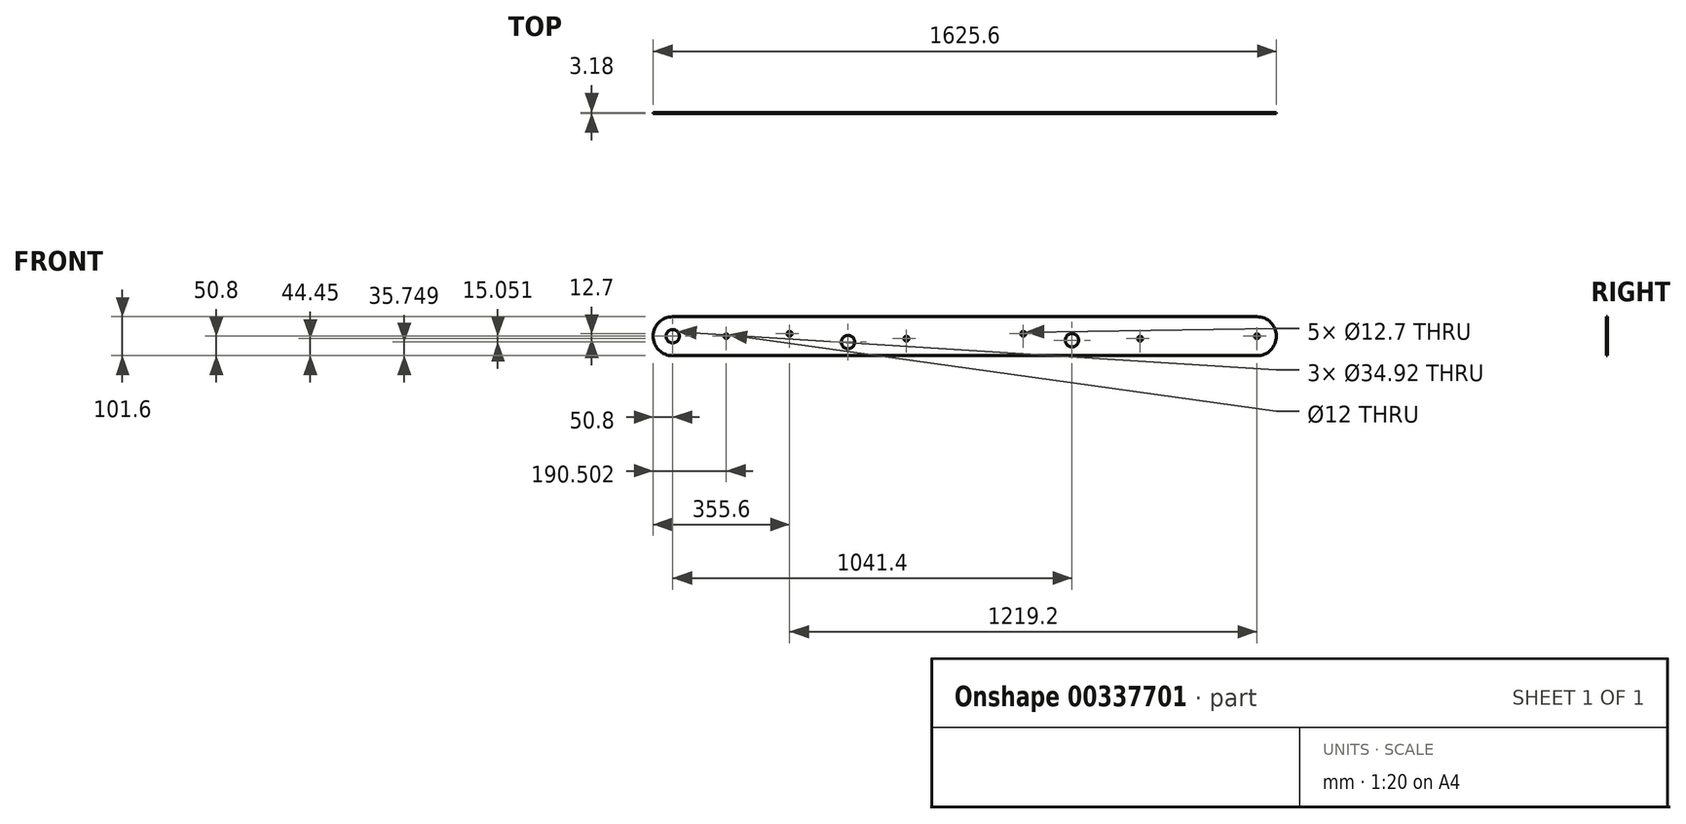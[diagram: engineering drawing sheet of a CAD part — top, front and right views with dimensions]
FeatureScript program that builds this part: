
annotation { "Feature Type Name" : "Feature", "Feature Type Description" : "" }
export const myFeature = defineFeature(function(context is Context, id is Id, definition is map)
    precondition{}
    {
        {
            var Q0;
            Q0=qCreatedBy(makeId("Front.planeOp"),FACE);
            var sketch = newSketch(context, id + "F0", { "sketchPlane" : qUnion([Q0])});
            skLineSegment(sketch, "E0.bottom", {"start": v(0, 0) * mm, "end": v(0, 0) * mm});
            skLineSegment(sketch, "E0.top", {"start": v(0, -101.6) * mm, "end": v(0, -101.6) * mm});
            skLineSegment(sketch, "E1.bottom", {"start": v(1524, -101.6) * mm, "end": v(0, -101.6) * mm});
            skLineSegment(sketch, "E1.top", {"start": v(1524, 0) * mm, "end": v(0, 0) * mm});
            skLineSegment(sketch, "E1.left", {"start": v(1524, -101.6) * mm, "end": v(1524, 0) * mm});
            skArc(sketch, "E2", {"start": v(1524, -101.6) * mm, "mid": v(1574.8, -50.8) * mm, "end": v(1524, 0) * mm});
            skArc(sketch, "E3", {"start": v(0, 0) * mm, "mid": v(-50.8, -50.8) * mm, "end": v(0, -101.6) * mm});
            skCircle(sketch, "E4", {"center": v(1219.2, -57.15) * mm, "radius": 6.35 * mm});
            skCircle(sketch, "E5", {"center": v(914.4, -44.45) * mm, "radius": 6.35 * mm});
            skCircle(sketch, "E6", {"center": v(0, -50.8) * mm, "radius": 17.46 * mm});
            skCircle(sketch, "E7", {"center": v(1524, -50.8) * mm, "radius": 6.35 * mm});
            skCircle(sketch, "E8", {"center": v(609.6, -57.15) * mm, "radius": 6.35 * mm});
            skCircle(sketch, "E9", {"center": v(304.8, -44.45) * mm, "radius": 6.35 * mm});
            skCircle(sketch, "E10", {"center": v(139.7, -50.8) * mm, "radius": 6 * mm});
            skCircle(sketch, "E11", {"center": v(457.2, -65.85) * mm, "radius": 17.46 * mm});
            skCircle(sketch, "E12", {"center": v(1041.4, -61.36) * mm, "radius": 17.46 * mm});
            skLineSegment(sketch, "E13", {"start": v(139.7, -50.8) * mm, "end": v(17.46, -50.8) * mm});
            skLineSegment(sketch, "E14.trimOffspring", {"start": v(-17.46, -50.8) * mm, "end": v(-50.8, -50.8) * mm});
            skSolve(sketch);
        }
        {
            var Q0;
            Q0=makeQuery(id+"F0.imprint","IMPRINT",FACE,{"disambiguationData":[TD([[makeQuery(id+"F0.imprint","IMPRINT",EDGE,{"derivedFrom":sQuery(id+"F0.wireOp",EDGE,"E1.bottom")}),-1.0]])]});
            var Q1;
            Q1=makeQuery(id+"F0.imprint","IMPRINT",FACE,{"disambiguationData":[TD([[makeQuery(id+"F0.imprint","IMPRINT",EDGE,{"derivedFrom":sQuery(id+"F0.wireOp",EDGE,"E1.left")}),-1.0]])]});
            var Q2;
            Q2=makeQuery(id+"F0.imprint","IMPRINT",FACE,{"disambiguationData":[TD([[makeQuery(id+"F0.imprint","IMPRINT",EDGE,{"derivedFrom":sQuery(id+"F0.wireOp",EDGE,"E1.right")}),1.0]])]});
            extrude(context, id + "F1", {"entities" : qUnion([Q0, Q1, Q2]), "depth" : 3.17 * mm});
        }
    });
